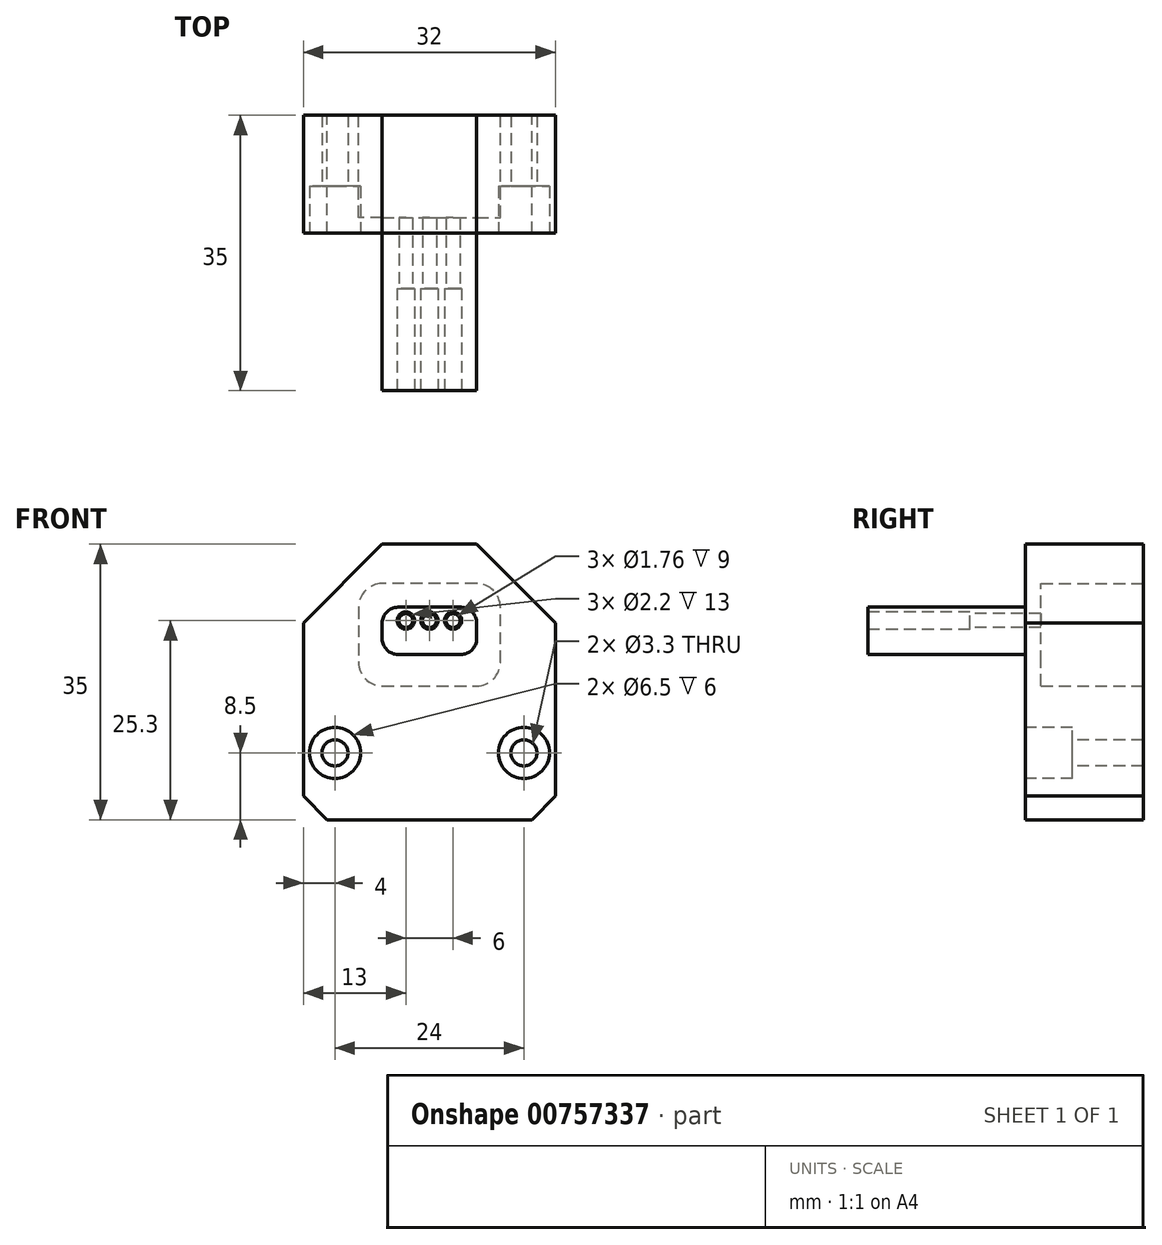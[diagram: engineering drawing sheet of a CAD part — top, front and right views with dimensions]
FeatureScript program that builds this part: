
annotation { "Feature Type Name" : "Feature", "Feature Type Description" : "" }
export const myFeature = defineFeature(function(context is Context, id is Id, definition is map)
    precondition{}
    {
        {
            var Q0;
            Q0=qCreatedBy(makeId("Front.planeOp"),FACE);
            var sketch = newSketch(context, id + "F0", { "sketchPlane" : qUnion([Q0])});
            skLineSegment(sketch, "E0.bottom", {"start": v(10, 0) * mm, "end": v(22, 0) * mm});
            skLineSegment(sketch, "E0.top", {"start": v(3, -35) * mm, "end": v(29, -35) * mm});
            skLineSegment(sketch, "E0.left", {"start": v(0, -10) * mm, "end": v(0, -32) * mm});
            skLineSegment(sketch, "E0.right", {"start": v(32, -10) * mm, "end": v(32, -32) * mm});
            skPoint(sketch, "E1", {"position": v(0, -10) * mm});
            skPoint(sketch, "E2", {"position": v(10, 0) * mm});
            skPoint(sketch, "E3", {"position": v(22, 0) * mm});
            skPoint(sketch, "E4", {"position": v(32, -10) * mm});
            skPoint(sketch, "E5", {"position": v(32, -32) * mm});
            skPoint(sketch, "E6", {"position": v(0, -32) * mm});
            skPoint(sketch, "E7", {"position": v(3, -35) * mm});
            skPoint(sketch, "E8", {"position": v(29, -35) * mm});
            skLineSegment(sketch, "E9", {"start": v(0, -10) * mm, "end": v(10, 0) * mm});
            skLineSegment(sketch, "E10", {"start": v(22, 0) * mm, "end": v(32, -10) * mm});
            skLineSegment(sketch, "E11", {"start": v(32, -32) * mm, "end": v(29, -35) * mm});
            skLineSegment(sketch, "E12", {"start": v(0, -32) * mm, "end": v(3, -35) * mm});
            skPoint(sketch, "E13.orphan", {"position": v(0, 0) * mm});
            skPoint(sketch, "E14.orphan", {"position": v(32, 0) * mm});
            skPoint(sketch, "E15.orphan", {"position": v(32, -35) * mm});
            skPoint(sketch, "E16.orphan", {"position": v(0, -35) * mm});
            skSolve(sketch);
        }
        {
            var Q0;
            Q0=makeQuery(id+"F0.imprint","IMPRINT",FACE,{"disambiguationData":[TD([[makeQuery(id+"F0.imprint","IMPRINT",EDGE,{"derivedFrom":sQuery(id+"F0.wireOp",EDGE,"E0.bottom")}),-1.0]])]});
            extrude(context, id + "F1", {"entities" : qUnion([Q0]), "depth" : 15 * mm, "offsetDistance" : 25 * mm});
        }
        {
            var Q0;
            Q0=makeQuery(id+"F1.opExtrude","CAP_FACE",FACE,{"disambiguationData":[OSD([sQuery(id+"F0.wireOp",EDGE,"E0.bottom"),sQuery(id+"F0.wireOp",EDGE,"E0.top"),sQuery(id+"F0.wireOp",EDGE,"E0.left"),sQuery(id+"F0.wireOp",EDGE,"E0.right"),sQuery(id+"F0.wireOp",EDGE,"E9"),sQuery(id+"F0.wireOp",EDGE,"E10"),sQuery(id+"F0.wireOp",EDGE,"E11"),sQuery(id+"F0.wireOp",EDGE,"E12")])],"isStart":false});
            var sketch = newSketch(context, id + "F2", { "sketchPlane" : qUnion([Q0])});
            skPoint(sketch, "E17", {"position": v(10, -8) * mm});
            skPoint(sketch, "E18", {"position": v(22, -8) * mm});
            skPoint(sketch, "E19", {"position": v(22, -14) * mm});
            skPoint(sketch, "E20", {"position": v(10, -14) * mm});
            skPoint(sketch, "E21", {"position": v(4, -26.5) * mm});
            skPoint(sketch, "E22", {"position": v(28, -26.5) * mm});
            skLineSegment(sketch, "E23", {"start": v(10, -8) * mm, "end": v(22, -8) * mm});
            skLineSegment(sketch, "E24", {"start": v(22, -8) * mm, "end": v(22, -14) * mm});
            skLineSegment(sketch, "E25", {"start": v(22, -14) * mm, "end": v(10, -14) * mm});
            skLineSegment(sketch, "E26", {"start": v(10, -14) * mm, "end": v(10, -8) * mm});
            skSolve(sketch);
        }
        {
            var Q0;
            Q0=makeQuery(id+"F2.imprint","IMPRINT",FACE,{"disambiguationData":[TD([[makeQuery(id+"F2.imprint","IMPRINT",EDGE,{"derivedFrom":sQuery(id+"F2.wireOp",EDGE,"E23")}),-1.0]])]});
            extrude(context, id + "F3", {"entities" : qUnion([Q0]), "operationType" : NewBodyOperationType.ADD, "depth" : (20) * mm, "offsetDistance" : 25 * mm});
        }
        {
            var Q0;
            Q0=makeQuery(id+"F1.opExtrude","CAP_FACE",FACE,{"disambiguationData":[OSD([sQuery(id+"F0.wireOp",EDGE,"E0.bottom"),sQuery(id+"F0.wireOp",EDGE,"E0.top"),sQuery(id+"F0.wireOp",EDGE,"E0.left"),sQuery(id+"F0.wireOp",EDGE,"E0.right"),sQuery(id+"F0.wireOp",EDGE,"E9"),sQuery(id+"F0.wireOp",EDGE,"E10"),sQuery(id+"F0.wireOp",EDGE,"E11"),sQuery(id+"F0.wireOp",EDGE,"E12")])],"isStart":true});
            var sketch = newSketch(context, id + "F4", { "sketchPlane" : qUnion([Q0])});
            skPoint(sketch, "E27", {"position": v(-25, -5) * mm});
            skPoint(sketch, "E28", {"position": v(-7, -5) * mm});
            skPoint(sketch, "E29", {"position": v(-7, -18) * mm});
            skPoint(sketch, "E30", {"position": v(-25, -18) * mm});
            skLineSegment(sketch, "E31", {"start": v(-25, -5) * mm, "end": v(-7, -5) * mm});
            skLineSegment(sketch, "E32", {"start": v(-7, -18) * mm, "end": v(-25, -18) * mm});
            skLineSegment(sketch, "E33", {"start": v(-25, -18) * mm, "end": v(-25, -5) * mm});
            skLineSegment(sketch, "E34", {"start": v(-7, -5) * mm, "end": v(-7, -18) * mm});
            skSolve(sketch);
        }
        {
            var Q0;
            Q0=makeQuery(id+"F4.imprint","IMPRINT",FACE,{"disambiguationData":[TD([[makeQuery(id+"F4.imprint","IMPRINT",EDGE,{"derivedFrom":sQuery(id+"F4.wireOp",EDGE,"E31")}),-1.0]])]});
            extrude(context, id + "F5", {"entities" : qUnion([Q0]), "operationType" : NewBodyOperationType.REMOVE, "oppositeDirection" : true, "depth" : 13 * mm, "offsetDistance" : 25 * mm});
        }
        {
            var Q0;
            Q0=makeQuery(id+"F5.boolean.opBoolean","COPY",EDGE,{"derivedFrom":makeQuery(id+"F5.opExtrude","SWEPT_EDGE",EDGE,{"disambiguationData":[OSD([sQuery(id+"F4.wireOp",EDGE,"E31"),sQuery(id+"F4.wireOp",EDGE,"E33")])]})});
            var Q1;
            Q1=makeQuery(id+"F5.boolean.opBoolean","COPY",EDGE,{"derivedFrom":makeQuery(id+"F5.opExtrude","SWEPT_EDGE",EDGE,{"disambiguationData":[OSD([sQuery(id+"F4.wireOp",EDGE,"E31"),sQuery(id+"F4.wireOp",EDGE,"E34")])]})});
            var Q2;
            Q2=makeQuery(id+"F5.boolean.opBoolean","COPY",EDGE,{"derivedFrom":makeQuery(id+"F5.opExtrude","SWEPT_EDGE",EDGE,{"disambiguationData":[OSD([sQuery(id+"F4.wireOp",EDGE,"E32"),sQuery(id+"F4.wireOp",EDGE,"E33")])]})});
            var Q3;
            Q3=makeQuery(id+"F5.boolean.opBoolean","COPY",EDGE,{"derivedFrom":makeQuery(id+"F5.opExtrude","SWEPT_EDGE",EDGE,{"disambiguationData":[OSD([sQuery(id+"F4.wireOp",EDGE,"E32"),sQuery(id+"F4.wireOp",EDGE,"E34")])]})});
            fillet(context, id + "F6", {"entities" : qUnion([Q0, Q1, Q2, Q3]), "radius" : 3 * mm, "tangentPropagation" : true, "allowEdgeOverflow" : false});
        }
        {
            var Q0;
            Q0=sQuery(id+"F2.wireOp",VERTEX,"E21");
            var Q1;
            Q1=sQuery(id+"F2.wireOp",VERTEX,"E22");
            var Q2;
            Q2=makeQuery(id+"F1.opExtrude","SWEPT_BODY",BODY,{"disambiguationData":[OSD([sQuery(id+"F0.wireOp",EDGE,"E0.bottom"),sQuery(id+"F0.wireOp",EDGE,"E0.top"),sQuery(id+"F0.wireOp",EDGE,"E0.left"),sQuery(id+"F0.wireOp",EDGE,"E0.right"),sQuery(id+"F0.wireOp",EDGE,"E9"),sQuery(id+"F0.wireOp",EDGE,"E10"),sQuery(id+"F0.wireOp",EDGE,"E11"),sQuery(id+"F0.wireOp",EDGE,"E12")])]});
            hole(context, id + "F7", {"style" : HoleStyle.C_BORE, "endStyle" : HoleEndStyle.THROUGH, "holeDiameter" : 3.3 * mm, "cBoreDiameter" : 6.5 * mm, "cBoreDepth" : 6 * mm, "majorDiameter" : 5 * mm, "isTappedThrough" : true, "tappedDepth" : 13.25 * mm, "tapClearance" : 3, "locations" : qUnion([Q0, Q1]), "scope" : qUnion([Q2])});
        }
        {
            var Q0;
            Q0=makeQuery(id+"F3.opExtrude","CAP_FACE",FACE,{"disambiguationData":[OSD([sQuery(id+"F2.wireOp",EDGE,"E23"),sQuery(id+"F2.wireOp",EDGE,"E24"),sQuery(id+"F2.wireOp",EDGE,"E25"),sQuery(id+"F2.wireOp",EDGE,"E26")])],"isStart":false});
            var sketch = newSketch(context, id + "F8", { "sketchPlane" : qUnion([Q0])});
            skPoint(sketch, "E35", {"position": v(19.06, -8) * mm});
            skPoint(sketch, "E36", {"position": v(19, -9.7) * mm});
            skPoint(sketch, "E37", {"position": v(16, -9.7) * mm});
            skPoint(sketch, "E38", {"position": v(13, -9.7) * mm});
            skSolve(sketch);
        }
        {
            var Q0;
            Q0=makeQuery(id+"F3.opExtrude","SWEPT_EDGE",EDGE,{"disambiguationData":[OSD([sQuery(id+"F2.wireOp",EDGE,"E23"),sQuery(id+"F2.wireOp",EDGE,"E24")])]});
            var Q1;
            Q1=makeQuery(id+"F3.opExtrude","SWEPT_EDGE",EDGE,{"disambiguationData":[OSD([sQuery(id+"F2.wireOp",EDGE,"E24"),sQuery(id+"F2.wireOp",EDGE,"E25")])]});
            var Q2;
            Q2=makeQuery(id+"F3.opExtrude","SWEPT_EDGE",EDGE,{"disambiguationData":[OSD([sQuery(id+"F2.wireOp",EDGE,"E23"),sQuery(id+"F2.wireOp",EDGE,"E26")])]});
            var Q3;
            Q3=makeQuery(id+"F3.opExtrude","SWEPT_EDGE",EDGE,{"disambiguationData":[OSD([sQuery(id+"F2.wireOp",EDGE,"E25"),sQuery(id+"F2.wireOp",EDGE,"E26")])]});
            fillet(context, id + "F9", {"entities" : qUnion([Q0, Q1, Q2, Q3]), "radius" : 2 * mm, "tangentPropagation" : true, "allowEdgeOverflow" : false});
        }
        {
            var Q0;
            Q0=sQuery(id+"F8.wireOp",VERTEX,"E36");
            var Q1;
            Q1=sQuery(id+"F8.wireOp",VERTEX,"E37");
            var Q2;
            Q2=sQuery(id+"F8.wireOp",VERTEX,"E38");
            var Q3;
            Q3=makeQuery(id+"F1.opExtrude","SWEPT_BODY",BODY,{"disambiguationData":[OSD([sQuery(id+"F0.wireOp",EDGE,"E0.bottom"),sQuery(id+"F0.wireOp",EDGE,"E0.top"),sQuery(id+"F0.wireOp",EDGE,"E0.left"),sQuery(id+"F0.wireOp",EDGE,"E0.right"),sQuery(id+"F0.wireOp",EDGE,"E9"),sQuery(id+"F0.wireOp",EDGE,"E10"),sQuery(id+"F0.wireOp",EDGE,"E11"),sQuery(id+"F0.wireOp",EDGE,"E12")])]});
            hole(context, id + "F10", {"style" : HoleStyle.C_BORE, "endStyle" : HoleEndStyle.THROUGH, "holeDiameter" : 1.76 * mm, "cBoreDiameter" : 2.2 * mm, "cBoreDepth" : 13 * mm, "majorDiameter" : 5 * mm, "isTappedThrough" : true, "tappedDepth" : 13.25 * mm, "tapClearance" : 3, "locations" : qUnion([Q0, Q1, Q2]), "scope" : qUnion([Q3])});
        }
    });
